# Revit family: Storage-Mounted-Teknion-BOKG_Cubic_Overhead_Cabinet_Glass_Doors-R2015
name_source: partatom
category: Casework
revit_build: Autodesk Revit Architecture 2015 (Build: 20140323_1530(x64)
units: mm (PartAtom-declared; Revit-internal decimal feet)

## types (2) — shared parameters
Assembly Code = E2020200
Depth = 18 "
Manufacturer = Teknion
Manufacturer Fax = 416.661.4586
Part Number = BOKG
Product Documentation Link = http://www.teknion.com
Product Line = Expansion Casegoods
Product Page URL = http://www.teknion.com
Series = Expansion Casegoods
Sustainability Data = http://www.teknion.com
URL = http://www.teknion.com
Unit Weight URL = http://www.teknion.com
Warranty = http://www.teknion.com

## per-type parameters (varying)
| type | Actual Height | Description | Height | Model |
| 16" High | 15.898 " | Overhead Cabinet – Glass Hinged Doors, 18" Depth, 16" Height | 16 " | BOKGB18_16 |
| 18" High | 17.976 " | Overhead Cabinet – Glass Hinged Doors, 18" Depth, 18" Height | 18 " | BOKGB18_18 |

## geometry (parser evidence)
native form markers: Blend x136, Sweep x3
no freeform markers — native parametric forms only
